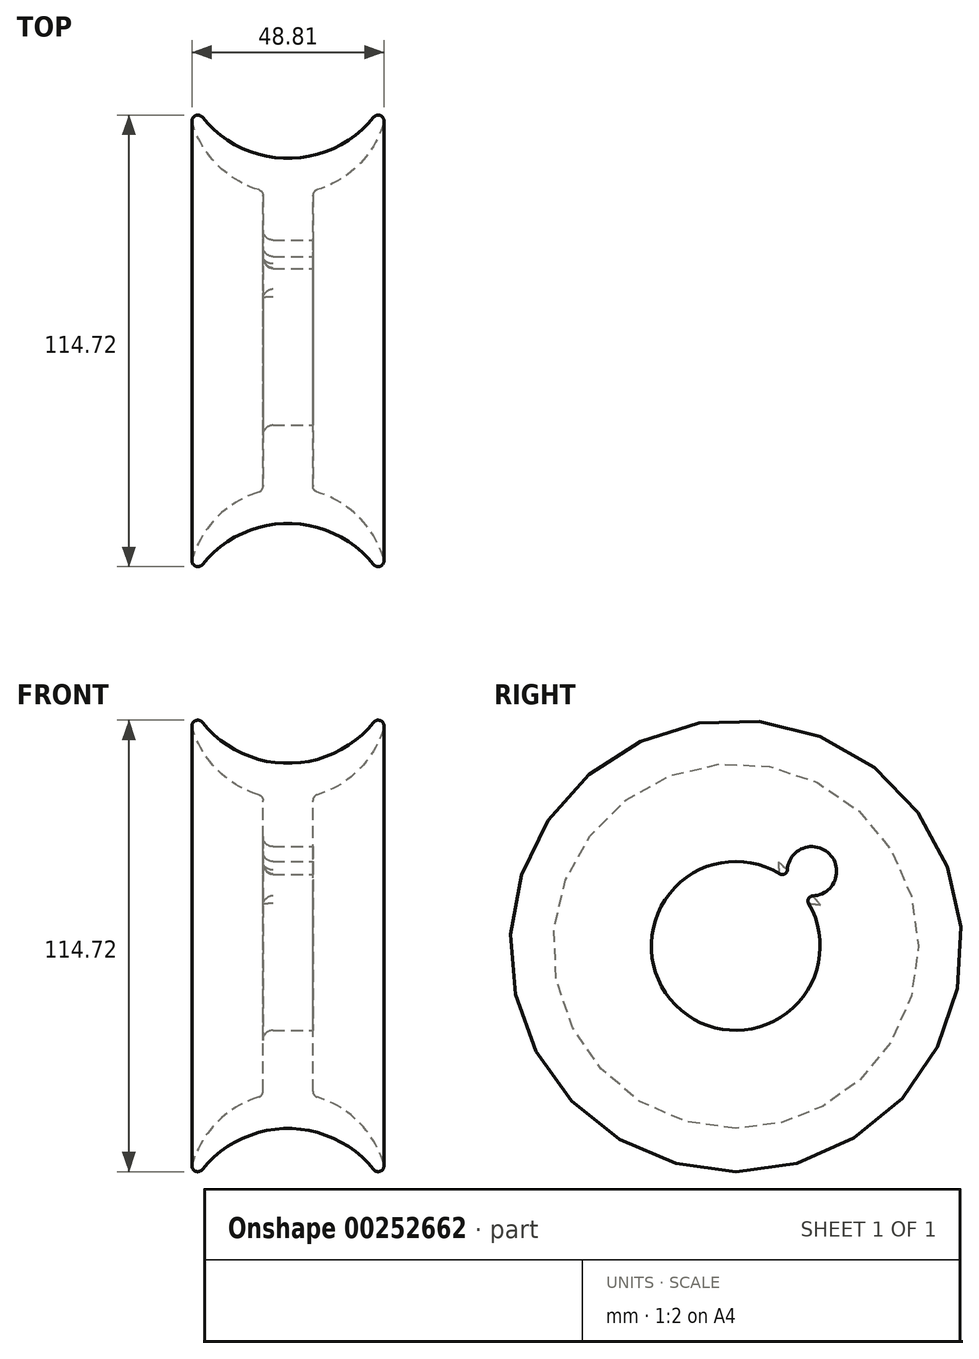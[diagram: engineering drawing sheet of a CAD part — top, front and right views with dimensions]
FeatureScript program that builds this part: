
annotation { "Feature Type Name" : "Feature", "Feature Type Description" : "" }
export const myFeature = defineFeature(function(context is Context, id is Id, definition is map)
    precondition{}
    {
        {
            var Q0;
            Q0=qCreatedBy(makeId("Front.planeOp"),FACE);
            var sketch = newSketch(context, id + "F0", { "sketchPlane" : qUnion([Q0])});
            skLineSegment(sketch, "E0", {"start": v(-5.68, 36.97) * mm, "end": v(-5.68, 11.93) * mm});
            skLineSegment(sketch, "E1", {"start": v(-7.17, 0) * mm, "end": v(-16.9, 0) * mm});
            skLineSegment(sketch, "E2", {"start": v(-18.38, 11.93) * mm, "end": v(-18.38, 36.97) * mm});
            skArc(sketch, "E3", {"start": v(-4.63, 38.4) * mm, "mid": v(5.99, 44.8) * mm, "end": v(12.31, 55.44) * mm});
            skArc(sketch, "E4", {"start": v(-33.79, 56.8) * mm, "mid": v(-12.03, 46.4) * mm, "end": v(9.72, 56.8) * mm});
            skArc(sketch, "E5.trimOffspring", {"start": v(-36.37, 55.44) * mm, "mid": v(-30.05, 44.8) * mm, "end": v(-19.44, 38.4) * mm});
            skPoint(sketch, "E6.visualSharp", {"position": v(-37.43, 62.7) * mm});
            skArc(sketch, "E6.filletArc", {"start": v(-33.79, 56.8) * mm, "mid": v(-35.64, 57.19) * mm, "end": v(-36.37, 55.44) * mm});
            skPoint(sketch, "E7.visualSharp", {"position": v(13.37, 62.7) * mm});
            skArc(sketch, "E7.filletArc", {"start": v(12.31, 55.44) * mm, "mid": v(11.58, 57.19) * mm, "end": v(9.72, 56.8) * mm});
            skPoint(sketch, "E8.visualSharp", {"position": v(-18.38, 38.1) * mm});
            skArc(sketch, "E8.filletArc", {"start": v(-18.38, 36.97) * mm, "mid": v(-18.67, 37.86) * mm, "end": v(-19.44, 38.4) * mm});
            skPoint(sketch, "E9.visualSharp", {"position": v(-5.68, 38.1) * mm});
            skArc(sketch, "E9.filletArc", {"start": v(-4.63, 38.4) * mm, "mid": v(-5.39, 37.86) * mm, "end": v(-5.68, 36.97) * mm});
            skLineSegment(sketch, "E10", {"start": v(-16.9, 10.44) * mm, "end": v(-7.17, 10.44) * mm});
            skPoint(sketch, "E11.visualSharp", {"position": v(-18.38, 10.44) * mm});
            skArc(sketch, "E11.filletArc", {"start": v(-18.38, 11.93) * mm, "mid": v(-17.95, 10.87) * mm, "end": v(-16.9, 10.44) * mm});
            skPoint(sketch, "E12.visualSharp", {"position": v(-5.68, 10.44) * mm});
            skArc(sketch, "E12.filletArc", {"start": v(-7.17, 10.44) * mm, "mid": v(-6.12, 10.87) * mm, "end": v(-5.68, 11.93) * mm});
            skSolve(sketch);
        }
        {
            var Q0;
            Q0=makeQuery(id+"F0.imprint","IMPRINT",FACE,{"disambiguationData":[TD([[makeQuery(id+"F0.imprint","IMPRINT",EDGE,{"derivedFrom":sQuery(id+"F0.wireOp",EDGE,"E0")}),-1.0]])]});
            var Q1;
            Q1=sQuery(id+"F0.wireOp",EDGE,"E1");
            revolve(context, id + "F1", {"entities" : qUnion([Q0]), "axis" : qUnion([Q1]), "revolveType" : RevolveType.FULL});
        }
        {
            var Q0;
            Q0=makeQuery(id+"F1.opRevolve","SWEPT_FACE",FACE,{"disambiguationData":[OSD([sQuery(id+"F0.wireOp",EDGE,"E0")])]});
            var sketch = newSketch(context, id + "F2", { "sketchPlane" : qUnion([Q0])});
            skArc(sketch, "E13", {"start": v(13.56, 16.61) * mm, "mid": v(-15.32, -15) * mm, "end": v(16.89, 13.21) * mm});
            skArc(sketch, "E14", {"start": v(16.89, 13.21) * mm, "mid": v(23.84, 23.35) * mm, "end": v(13.56, 16.61) * mm});
            skPoint(sketch, "E14.first.point", {"position": v(16.89, 13.21) * mm});
            skPoint(sketch, "E14.second.point", {"position": v(25.62, 19.3) * mm});
            skPoint(sketch, "E14.third.point", {"position": v(24.35, 15.18) * mm});
            skSolve(sketch);
        }
        {
            var Q0;
            Q0=makeQuery(id+"F2.imprint","IMPRINT",FACE,{"disambiguationData":[TD([[makeQuery(id+"F2.imprint","IMPRINT",EDGE,{"derivedFrom":makeQuery(id+"F1.opRevolve","SWEPT_EDGE",EDGE,{"disambiguationData":[OSD([sQuery(id+"F0.wireOp",EDGE,"E0"),sQuery(id+"F0.wireOp",EDGE,"E12.filletArc")])]})}),1.0]])]});
            var Q1;
            Q1=makeQuery(id+"F2.imprint","IMPRINT",FACE,{"disambiguationData":[TD([[makeQuery(id+"F2.imprint","IMPRINT",EDGE,{"derivedFrom":sQuery(id+"F2.wireOp",EDGE,"E13")}),1.0]])]});
            extrude(context, id + "F3", {"entities" : qUnion([Q0, Q1]), "operationType" : NewBodyOperationType.REMOVE, "oppositeDirection" : true, "depth" : 25.4 * mm});
        }
        {
            var Q0;
            Q0=makeQuery(id+"F3.boolean.opBoolean","COPY",EDGE,{"derivedFrom":makeQuery(id+"F3.opExtrude","CAP_EDGE",EDGE,{"disambiguationData":[OSD([sQuery(id+"F2.wireOp",EDGE,"E14")])],"isStart":true})});
            var Q1;
            Q1=makeQuery(id+"F3.boolean.opBoolean","COPY",EDGE,{"derivedFrom":makeQuery(id+"F3.opExtrude","CAP_EDGE",EDGE,{"disambiguationData":[OSD([sQuery(id+"F2.wireOp",EDGE,"E13")])],"isStart":true})});
            var Q2;
            Q2=makeQuery(id+"F3.boolean.opBoolean","INTERSECT",EDGE,{"derivedFrom":[makeQuery(id+"F1.opRevolve","SWEPT_FACE",FACE,{"disambiguationData":[OSD([sQuery(id+"F0.wireOp",EDGE,"E2")])]}),makeQuery(id+"F3.opExtrude","SWEPT_FACE",FACE,{"disambiguationData":[OSD([sQuery(id+"F2.wireOp",EDGE,"E14")])]})]});
            var Q3;
            Q3=makeQuery(id+"F3.boolean.opBoolean","INTERSECT",EDGE,{"derivedFrom":[makeQuery(id+"F1.opRevolve","SWEPT_FACE",FACE,{"disambiguationData":[OSD([sQuery(id+"F0.wireOp",EDGE,"E2")])]}),makeQuery(id+"F3.opExtrude","SWEPT_FACE",FACE,{"disambiguationData":[OSD([sQuery(id+"F2.wireOp",EDGE,"E13")])]})]});
            fillet(context, id + "F4", {"entities" : qUnion([Q0, Q1, Q2, Q3]), "radius" : 2.54 * mm, "tangentPropagation" : true, "allowEdgeOverflow" : false});
        }
        {
            var Q0;
            {var subQ0=sQuery(id+"F2.wireOp",EDGE,"E14");var subQ1=sQuery(id+"F2.wireOp",EDGE,"E13");Q0=makeQuery(id+"F3.boolean.opBoolean","COPY",EDGE,{"derivedFrom":makeQuery(id+"F3.opExtrude","SWEPT_EDGE",EDGE,{"disambiguationData":[OSD([subQ1,subQ0]),TDD([makeQuery(id+"F2.imprint","INTERSECT",VERTEX,{"disambiguationData":[OD(1.0)],"derivedFrom":[subQ1,subQ0]})])]})});}
            var Q1;
            {var subQ0=sQuery(id+"F2.wireOp",EDGE,"E14");var subQ1=sQuery(id+"F2.wireOp",EDGE,"E13");Q1=makeQuery(id+"F3.boolean.opBoolean","COPY",EDGE,{"derivedFrom":makeQuery(id+"F3.opExtrude","SWEPT_EDGE",EDGE,{"disambiguationData":[OSD([subQ1,subQ0]),TDD([makeQuery(id+"F2.imprint","INTERSECT",VERTEX,{"disambiguationData":[OD(0.0)],"derivedFrom":[subQ1,subQ0]})])]})});}
            fillet(context, id + "F5", {"entities" : qUnion([Q0, Q1]), "radius" : 1.27 * mm, "tangentPropagation" : true, "allowEdgeOverflow" : false});
        }
    });
